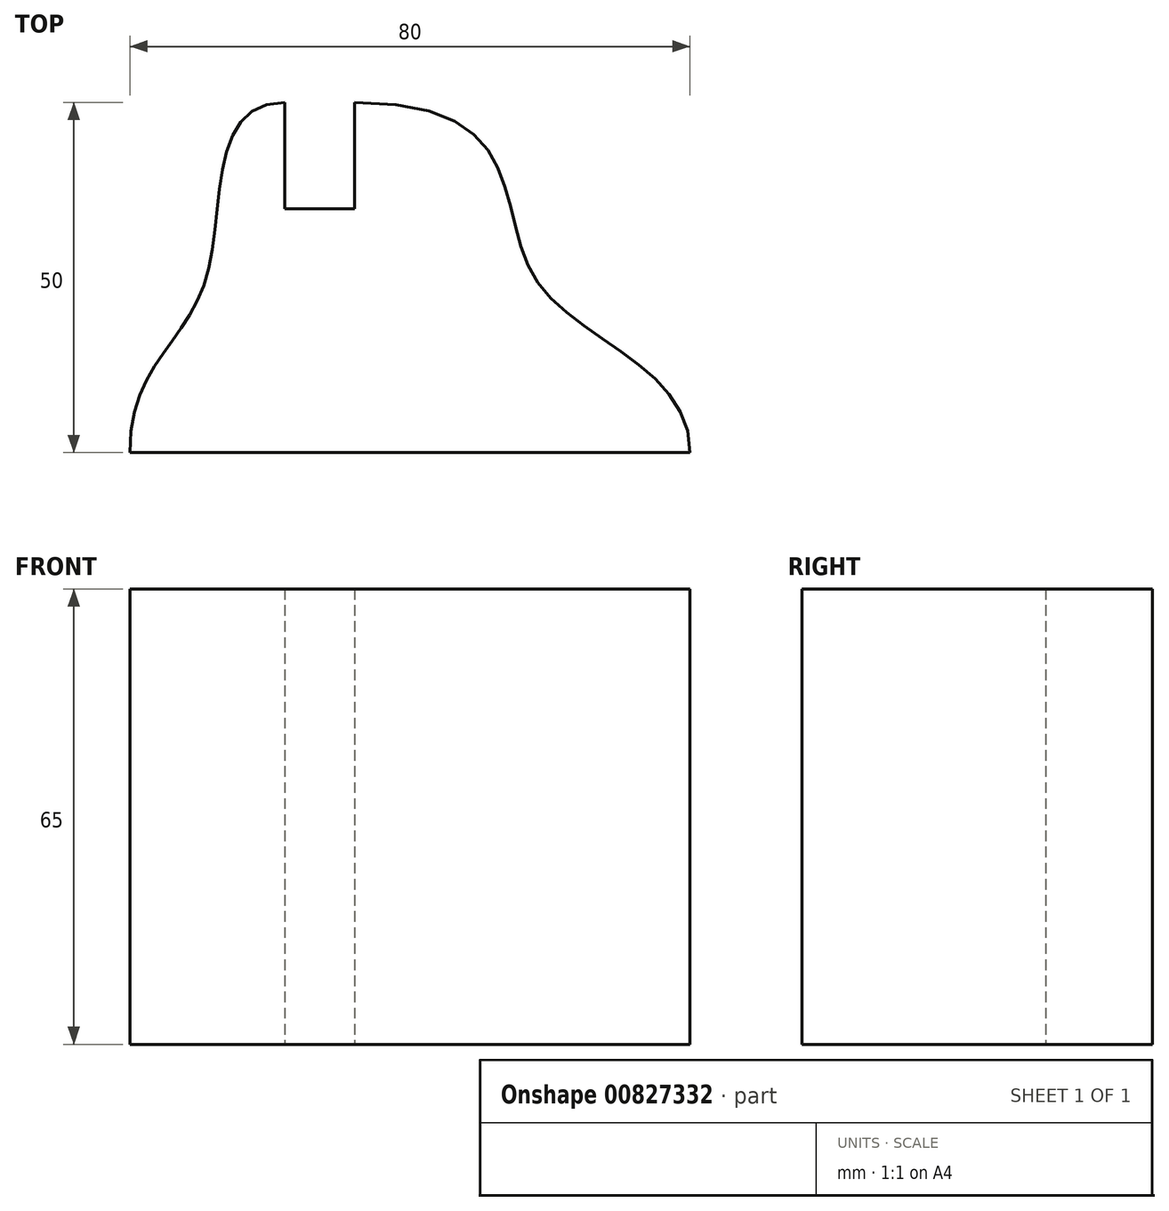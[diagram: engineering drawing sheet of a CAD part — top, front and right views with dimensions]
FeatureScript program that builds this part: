
annotation { "Feature Type Name" : "Feature", "Feature Type Description" : "" }
export const myFeature = defineFeature(function(context is Context, id is Id, definition is map)
    precondition{}
    {
        {
            var Q0;
            Q0=qCreatedBy(makeId("Top.planeOp"),FACE);
            var sketch = newSketch(context, id + "F0", { "sketchPlane" : qUnion([Q0])});
            skLineSegment(sketch, "E0", {"start": v(0, -25) * mm, "end": v(47.9, -25) * mm});
            skLineSegment(sketch, "E1", {"start": v(0, -25) * mm, "end": v(-32.1, -25) * mm});
            skFitSpline(sketch, "E2", {"points": [v(-10, 25) * mm, v(-21.18, 0) * mm, v(-32.1, -25) * mm], "startDerivative": vector(-67.02, 0) * mm, "endDerivative": vector(0, -75.07) * mm});
            skLineSegment(sketch, "E3", {"start": v(-10, 25) * mm, "end": v(-10, 9.8) * mm});
            skLineSegment(sketch, "E4", {"start": v(-10, 9.8) * mm, "end": v(0, 9.8) * mm});
            skLineSegment(sketch, "E5", {"start": v(0, 9.8) * mm, "end": v(0, 25) * mm});
            skFitSpline(sketch, "E6", {"points": [v(0, 25) * mm, v(25.66, 0) * mm, v(47.9, -25) * mm], "startDerivative": vector(151.37, 0) * mm, "endDerivative": vector(0, -76.3) * mm});
            skSolve(sketch);
        }
        {
            var Q0;
            Q0=makeQuery(id+"F0.imprint","IMPRINT",FACE,{"disambiguationData":[TD([[makeQuery(id+"F0.imprint","IMPRINT",EDGE,{"derivedFrom":sQuery(id+"F0.wireOp",EDGE,"E0")}),1.0]])]});
            extrude(context, id + "F1", {"entities" : qUnion([Q0]), "depth" : 65 * mm, "offsetDistance" : 25 * mm});
        }
    });
